SOLIDWORKS PART (.sldprt)
format: sldprt  version: not decoded by parser v0  size: 128,000 bytes
history: native  units: mm
features: sketch x4, plane x3, fillet x3, extrude x2, cut_extrude x2, material x1 (+13 scaffold rows collapsed)
feature tree (28):
  scaffold x13  (default folders/planes/origin — collapsed)
  material  "材质 <未指定>"
  plane  "前视基准面"
  plane  "上视基准面"
  plane  "右视基准面"
  sketch  "草图1"  dims[D1=40.0mm D2=10.0mm D3=0.2mm D4=0.2mm D5=0.1mm D6=0.1mm]
  extrude  "凸台-拉伸1"  Depth=20mm
  sketch  "草图2"
  extrude  "凸台-拉伸2"  Depth=20mm
  fillet  "圆角1"  Radius=15mm
  fillet  "圆角2"  Radius=5mm
  fillet  "圆角3"  Radius=3mm
  sketch  "草图3"  dims[D2=2.5mm D1=3.0mm]
  cut_extrude  "切除-拉伸1"  Depth=20mm
  sketch  "草图4"  dims[D1=8.0mm]
  cut_extrude  "切除-拉伸2"  [1 undecoded]
decode coverage: 9 of 11 modeling features carry decoded parameters
note: 1 parameter value undecoded
note: suppression state not decoded; provenance and decode notes live in map.json
